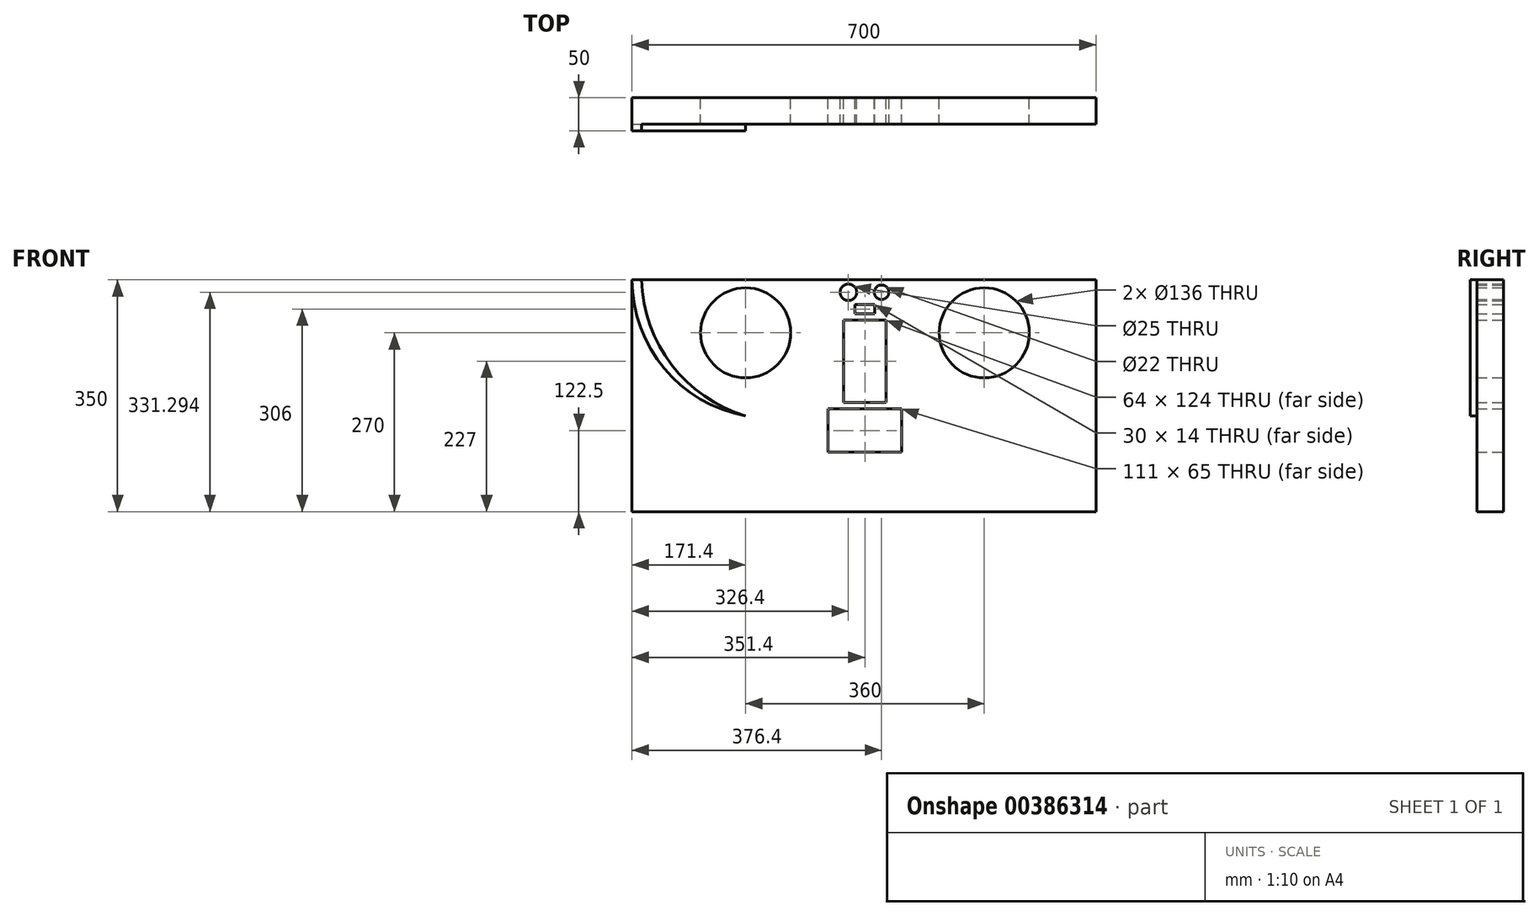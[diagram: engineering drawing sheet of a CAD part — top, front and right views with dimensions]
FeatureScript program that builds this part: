
annotation { "Feature Type Name" : "Feature", "Feature Type Description" : "" }
export const myFeature = defineFeature(function(context is Context, id is Id, definition is map)
    precondition{}
    {
        {
            var Q0;
            Q0=qCreatedBy(makeId("Front.planeOp"),FACE);
            var sketch = newSketch(context, id + "F0", { "sketchPlane" : qUnion([Q0])});
            skLineSegment(sketch, "E0.left", {"start": v(348.6, -144.5) * mm, "end": v(348.6, 205.5) * mm, "construction": true});
            skLineSegment(sketch, "E0.right", {"start": v(-351.4, -144.5) * mm, "end": v(-351.4, 205.5) * mm, "construction": true});
            skLineSegment(sketch, "E1", {"start": v(-351.4, 205.5) * mm, "end": v(-281.4, 205.5) * mm, "construction": true});
            skLineSegment(sketch, "E2", {"start": v(-281.4, 205.5) * mm, "end": v(-281.4, -74.5) * mm, "construction": true});
            skLineSegment(sketch, "E3", {"start": v(278.6, -74.5) * mm, "end": v(278.6, 205.5) * mm, "construction": true});
            skLineSegment(sketch, "E4", {"start": v(278.6, 205.5) * mm, "end": v(348.6, 205.5) * mm, "construction": true});
            skCircle(sketch, "E5", {"center": v(-180, 125.5) * mm, "radius": 68 * mm, "construction": true});
            skCircle(sketch, "E6", {"center": v(180, 125.5) * mm, "radius": 68 * mm, "construction": true});
            skLineSegment(sketch, "E7", {"start": v(0, 0) * mm, "end": v(0, 216.27) * mm, "construction": true});
            skLineSegment(sketch, "E8.bottom", {"start": v(15, 154.5) * mm, "end": v(-15, 154.5) * mm, "construction": true});
            skLineSegment(sketch, "E8.top", {"start": v(15, 168.5) * mm, "end": v(-15, 168.5) * mm, "construction": true});
            skLineSegment(sketch, "E8.left", {"start": v(15, 154.5) * mm, "end": v(15, 168.5) * mm, "construction": true});
            skLineSegment(sketch, "E8.right", {"start": v(-15, 154.5) * mm, "end": v(-15, 168.5) * mm, "construction": true});
            skPoint(sketch, "E8.middle", {"position": v(0, 161.5) * mm});
            skPoint(sketch, "E9.middle", {"position": v(0, 0) * mm});
            skCircle(sketch, "E10", {"center": v(-25, 186.8) * mm, "radius": 12.5 * mm, "construction": true});
            skCircle(sketch, "E11", {"center": v(25, 186.8) * mm, "radius": 11 * mm, "construction": true});
            skLineSegment(sketch, "E12.bottom", {"start": v(32, 20.5) * mm, "end": v(-32, 20.5) * mm, "construction": true});
            skLineSegment(sketch, "E12.top", {"start": v(32, 144.5) * mm, "end": v(-32, 144.5) * mm, "construction": true});
            skLineSegment(sketch, "E12.left", {"start": v(32, 20.5) * mm, "end": v(32, 144.5) * mm, "construction": true});
            skLineSegment(sketch, "E12.right", {"start": v(-32, 20.5) * mm, "end": v(-32, 144.5) * mm, "construction": true});
            skPoint(sketch, "E12.middle", {"position": v(0, 82.5) * mm});
            skLineSegment(sketch, "E13.bottom", {"start": v(55.5, -54.5) * mm, "end": v(-55.5, -54.5) * mm, "construction": true});
            skLineSegment(sketch, "E13.top", {"start": v(55.5, 10.5) * mm, "end": v(-55.5, 10.5) * mm, "construction": true});
            skLineSegment(sketch, "E13.left", {"start": v(55.5, -54.5) * mm, "end": v(55.5, 10.5) * mm, "construction": true});
            skLineSegment(sketch, "E13.right", {"start": v(-55.5, -54.5) * mm, "end": v(-55.5, 10.5) * mm, "construction": true});
            skPoint(sketch, "E13.middle", {"position": v(0, -22) * mm});
            skSolve(sketch);
        }
        {
            var Q0;
            Q0=qCreatedBy(makeId("Front.planeOp"),FACE);
            var sketch = newSketch(context, id + "F1", { "sketchPlane" : qUnion([Q0])});
            skLineSegment(sketch, "E14", {"start": v(-351.4, 205.5) * mm, "end": v(-351.4, -144.5) * mm});
            skLineSegment(sketch, "E15", {"start": v(348.6, -144.5) * mm, "end": v(348.6, 205.5) * mm});
            skLineSegment(sketch, "E16", {"start": v(348.6, 205.5) * mm, "end": v(278.6, 205.5) * mm});
            skLineSegment(sketch, "E17", {"start": v(-281.4, 205.5) * mm, "end": v(-351.4, 205.5) * mm});
            skLineSegment(sketch, "E18", {"start": v(-281.4, 205.5) * mm, "end": v(-281.4, -144.5) * mm});
            skLineSegment(sketch, "E19", {"start": v(-281.4, -144.5) * mm, "end": v(-351.4, -144.5) * mm});
            skLineSegment(sketch, "E20", {"start": v(278.6, 205.5) * mm, "end": v(278.6, -144.5) * mm});
            skLineSegment(sketch, "E21", {"start": v(278.6, -144.5) * mm, "end": v(348.6, -144.5) * mm});
            skLineSegment(sketch, "E22.bottom", {"start": v(-281.4, 205.5) * mm, "end": v(278.6, 205.5) * mm});
            skLineSegment(sketch, "E22.top", {"start": v(-281.4, -144.5) * mm, "end": v(278.6, -144.5) * mm});
            skCircle(sketch, "E23", {"center": v(-180, 125.5) * mm, "radius": 68 * mm});
            skCircle(sketch, "E24", {"center": v(180, 125.5) * mm, "radius": 68 * mm});
            skCircle(sketch, "E25", {"center": v(25, 186.8) * mm, "radius": 11 * mm});
            skCircle(sketch, "E26", {"center": v(-25, 186.8) * mm, "radius": 12.5 * mm});
            skLineSegment(sketch, "E27.bottom", {"start": v(32, 20.5) * mm, "end": v(-32, 20.5) * mm});
            skLineSegment(sketch, "E27.top", {"start": v(32, 144.5) * mm, "end": v(-32, 144.5) * mm});
            skLineSegment(sketch, "E27.left", {"start": v(32, 20.5) * mm, "end": v(32, 144.5) * mm});
            skLineSegment(sketch, "E27.right", {"start": v(-32, 20.5) * mm, "end": v(-32, 144.5) * mm});
            skPoint(sketch, "E27.middle", {"position": v(0, 82.5) * mm});
            skLineSegment(sketch, "E28.bottom", {"start": v(15, 154.5) * mm, "end": v(-15, 154.5) * mm});
            skLineSegment(sketch, "E28.top", {"start": v(15, 168.5) * mm, "end": v(-15, 168.5) * mm});
            skLineSegment(sketch, "E28.left", {"start": v(15, 154.5) * mm, "end": v(15, 168.5) * mm});
            skLineSegment(sketch, "E28.right", {"start": v(-15, 154.5) * mm, "end": v(-15, 168.5) * mm});
            skPoint(sketch, "E28.middle", {"position": v(0, 161.5) * mm});
            skLineSegment(sketch, "E29.bottom", {"start": v(55.5, -54.5) * mm, "end": v(-55.5, -54.5) * mm});
            skLineSegment(sketch, "E29.top", {"start": v(55.5, 10.5) * mm, "end": v(-55.5, 10.5) * mm});
            skLineSegment(sketch, "E29.left", {"start": v(55.5, -54.5) * mm, "end": v(55.5, 10.5) * mm});
            skLineSegment(sketch, "E29.right", {"start": v(-55.5, -54.5) * mm, "end": v(-55.5, 10.5) * mm});
            skPoint(sketch, "E29.middle", {"position": v(0, -22) * mm});
            skSolve(sketch);
        }
        {
            var Q0;
            Q0=makeQuery(id+"F1.imprint","IMPRINT",FACE,{"disambiguationData":[TD([[makeQuery(id+"F1.imprint","IMPRINT",EDGE,{"derivedFrom":sQuery(id+"F1.wireOp",EDGE,"E22.bottom")}),-1.0]])]});
            extrude(context, id + "F2", {"entities" : qUnion([Q0]), "depth" : 40 * mm});
        }
        {
            var Q0;
            Q0=makeQuery(id+"F1.imprint","IMPRINT",FACE,{"disambiguationData":[TD([[makeQuery(id+"F1.imprint","IMPRINT",EDGE,{"derivedFrom":sQuery(id+"F1.wireOp",EDGE,"E14")}),1.0]])]});
            var Q1;
            Q1=makeQuery(id+"F1.imprint","IMPRINT",FACE,{"disambiguationData":[TD([[makeQuery(id+"F1.imprint","IMPRINT",EDGE,{"derivedFrom":sQuery(id+"F1.wireOp",EDGE,"E15")}),1.0]])]});
            extrude(context, id + "F3", {"entities" : qUnion([Q0, Q1]), "operationType" : NewBodyOperationType.ADD, "depth" : 40 * mm});
        }
        {
            var Q0;
            Q0=makeQuery(id+"F1.imprint","IMPRINT",FACE,{"disambiguationData":[TD([[makeQuery(id+"F1.imprint","IMPRINT",EDGE,{"derivedFrom":sQuery(id+"F1.wireOp",EDGE,"E23")}),1.0]])]});
            var Q1;
            Q1=makeQuery(id+"F1.imprint","IMPRINT",FACE,{"disambiguationData":[TD([[makeQuery(id+"F1.imprint","IMPRINT",EDGE,{"derivedFrom":sQuery(id+"F1.wireOp",EDGE,"E24")}),1.0]])]});
            var Q2;
            Q2=makeQuery(id+"F1.imprint","IMPRINT",FACE,{"disambiguationData":[TD([[makeQuery(id+"F1.imprint","IMPRINT",EDGE,{"derivedFrom":sQuery(id+"F1.wireOp",EDGE,"E26")}),1.0]])]});
            var Q3;
            Q3=makeQuery(id+"F1.imprint","IMPRINT",FACE,{"disambiguationData":[TD([[makeQuery(id+"F1.imprint","IMPRINT",EDGE,{"derivedFrom":sQuery(id+"F1.wireOp",EDGE,"E25")}),1.0]])]});
            var Q4;
            Q4=makeQuery(id+"F1.imprint","IMPRINT",FACE,{"disambiguationData":[TD([[makeQuery(id+"F1.imprint","IMPRINT",EDGE,{"derivedFrom":sQuery(id+"F1.wireOp",EDGE,"E28.bottom")}),-1.0]])]});
            var Q5;
            Q5=makeQuery(id+"F1.imprint","IMPRINT",FACE,{"disambiguationData":[TD([[makeQuery(id+"F1.imprint","IMPRINT",EDGE,{"derivedFrom":sQuery(id+"F1.wireOp",EDGE,"E27.bottom")}),-1.0]])]});
            var Q6;
            Q6=makeQuery(id+"F1.imprint","IMPRINT",FACE,{"disambiguationData":[TD([[makeQuery(id+"F1.imprint","IMPRINT",EDGE,{"derivedFrom":sQuery(id+"F1.wireOp",EDGE,"E29.bottom")}),-1.0]])]});
            extrude(context, id + "F4", {"entities" : qUnion([Q0, Q1, Q2, Q3, Q4, Q5, Q6]), "operationType" : NewBodyOperationType.REMOVE, "oppositeDirection" : true, "depth" : 270 * mm});
        }
        {
            var Q0;
            {var subQ0=sQuery(id+"F1.wireOp",EDGE,"E20");var subQ1=sQuery(id+"F1.wireOp",EDGE,"E18");Q0=makeQuery(id+"F3.boolean.opBoolean","MERGE",FACE,{"derivedFrom":[makeQuery(id+"F2.opExtrude","CAP_FACE",FACE,{"disambiguationData":[OSD([sQuery(id+"F1.wireOp",EDGE,"E22.bottom"),sQuery(id+"F1.wireOp",EDGE,"E22.top"),subQ1,subQ0,sQuery(id+"F1.wireOp",EDGE,"E23"),sQuery(id+"F1.wireOp",EDGE,"E24"),sQuery(id+"F1.wireOp",EDGE,"E25"),sQuery(id+"F1.wireOp",EDGE,"E26"),sQuery(id+"F1.wireOp",EDGE,"E27.bottom"),sQuery(id+"F1.wireOp",EDGE,"E27.top"),sQuery(id+"F1.wireOp",EDGE,"E27.left"),sQuery(id+"F1.wireOp",EDGE,"E27.right"),sQuery(id+"F1.wireOp",EDGE,"E28.bottom"),sQuery(id+"F1.wireOp",EDGE,"E28.top"),sQuery(id+"F1.wireOp",EDGE,"E28.left"),sQuery(id+"F1.wireOp",EDGE,"E28.right"),sQuery(id+"F1.wireOp",EDGE,"E29.bottom"),sQuery(id+"F1.wireOp",EDGE,"E29.top"),sQuery(id+"F1.wireOp",EDGE,"E29.left"),sQuery(id+"F1.wireOp",EDGE,"E29.right")])],"isStart":false}),makeQuery(id+"F3.opExtrude","CAP_FACE",FACE,{"disambiguationData":[OSD([sQuery(id+"F1.wireOp",EDGE,"E14"),sQuery(id+"F1.wireOp",EDGE,"E17"),sQuery(id+"F1.wireOp",EDGE,"E19"),subQ1])],"isStart":false}),makeQuery(id+"F3.opExtrude","CAP_FACE",FACE,{"disambiguationData":[OSD([sQuery(id+"F1.wireOp",EDGE,"E15"),sQuery(id+"F1.wireOp",EDGE,"E16"),sQuery(id+"F1.wireOp",EDGE,"E21"),subQ0])],"isStart":false})]});}
            var sketch = newSketch(context, id + "F5", { "sketchPlane" : qUnion([Q0])});
            skPoint(sketch, "E30", {"position": v(-180, 125.5) * mm});
            skPoint(sketch, "E31", {"position": v(180, 125.5) * mm});
            skPoint(sketch, "E32", {"position": v(-180, 0) * mm});
            skPoint(sketch, "E33", {"position": v(180, 0) * mm});
            skPoint(sketch, "E34", {"position": v(-78.4, 205.5) * mm});
            skPoint(sketch, "E35", {"position": v(75.6, 205.5) * mm});
            skLineSegment(sketch, "E36", {"start": v(-78.4, 205.5) * mm, "end": v(-78.4, -144.5) * mm, "construction": true});
            skLineSegment(sketch, "E37", {"start": v(75.6, 205.5) * mm, "end": v(75.6, -144.5) * mm, "construction": true});
            skArc(sketch, "E38", {"start": v(-351.4, 205.5) * mm, "mid": v(-302.93, 71.7) * mm, "end": v(-180, 0) * mm});
            skArc(sketch, "E39", {"start": v(-180, 0) * mm, "mid": v(-299.3, -32.4) * mm, "end": v(-351.4, -144.5) * mm});
            skArc(sketch, "E40", {"start": v(-180, 0) * mm, "mid": v(-105.19, 90.88) * mm, "end": v(-78.4, 205.5) * mm});
            skArc(sketch, "E41", {"start": v(-78.4, -144.5) * mm, "mid": v(-106.34, -56.18) * mm, "end": v(-180, 0) * mm});
            skArc(sketch, "E42", {"start": v(180, 0) * mm, "mid": v(301.05, 72.6) * mm, "end": v(348.6, 205.5) * mm});
            skArc(sketch, "E43", {"start": v(348.6, -144.5) * mm, "mid": v(297.53, -33.48) * mm, "end": v(180, 0) * mm});
            skArc(sketch, "E44", {"start": v(75.6, 205.5) * mm, "mid": v(103.2, 90.25) * mm, "end": v(180, 0) * mm});
            skArc(sketch, "E45", {"start": v(180, 0) * mm, "mid": v(104.43, -55.36) * mm, "end": v(75.6, -144.5) * mm});
            skArc(sketch, "E46", {"start": v(-337.03, 205.5) * mm, "mid": v(-291.72, 77.38) * mm, "end": v(-180, 0) * mm});
            skArc(sketch, "E47", {"start": v(-180, 0) * mm, "mid": v(-260.12, -52.78) * mm, "end": v(-231.96, -144.5) * mm});
            skArc(sketch, "E48", {"start": v(-180, 0) * mm, "mid": v(-115.4, 92.85) * mm, "end": v(-105.19, 205.5) * mm});
            skPoint(sketch, "E48.endSnap0", {"position": v(-105.19, 90.88) * mm});
            skArc(sketch, "E49", {"start": v(-204.8, -144.5) * mm, "mid": v(-134.1, -82.25) * mm, "end": v(-180, 0) * mm});
            skArc(sketch, "E50", {"start": v(180, 0) * mm, "mid": v(287.56, 78.99) * mm, "end": v(330.04, 205.5) * mm});
            skPoint(sketch, "E51", {"position": v(102.38, 205.5) * mm});
            skArc(sketch, "E52", {"start": v(102.38, 205.5) * mm, "mid": v(113.85, 92.42) * mm, "end": v(180, 0) * mm});
            skArc(sketch, "E53", {"start": v(227.8, -144.5) * mm, "mid": v(256.43, -54.88) * mm, "end": v(180, 0) * mm});
            skArc(sketch, "E54", {"start": v(180, 0) * mm, "mid": v(133.6, -81.17) * mm, "end": v(202.37, -144.5) * mm});
            skLineSegment(sketch, "E55", {"start": v(-351.4, -144.5) * mm, "end": v(-231.96, -144.5) * mm});
            skLineSegment(sketch, "E56", {"start": v(-204.8, -144.5) * mm, "end": v(-78.4, -144.5) * mm});
            skLineSegment(sketch, "E57", {"start": v(-351.4, 205.5) * mm, "end": v(-337.03, 205.5) * mm});
            skLineSegment(sketch, "E58", {"start": v(-105.19, 205.5) * mm, "end": v(-78.4, 205.5) * mm});
            skLineSegment(sketch, "E59", {"start": v(75.6, 205.5) * mm, "end": v(102.38, 205.5) * mm});
            skLineSegment(sketch, "E60", {"start": v(330.04, 205.5) * mm, "end": v(348.6, 205.5) * mm});
            skLineSegment(sketch, "E61", {"start": v(75.6, -144.5) * mm, "end": v(202.37, -144.5) * mm});
            skLineSegment(sketch, "E62", {"start": v(227.8, -144.5) * mm, "end": v(348.6, -144.5) * mm});
            skSolve(sketch);
        }
        {
            var Q0;
            Q0=makeQuery(id+"F5.imprint","IMPRINT",FACE,{"disambiguationData":[TD([[makeQuery(id+"F5.imprint","IMPRINT",EDGE,{"derivedFrom":sQuery(id+"F5.wireOp",EDGE,"E38")}),1.0]])]});
            extrude(context, id + "F6", {"entities" : qUnion([Q0]), "operationType" : NewBodyOperationType.ADD, "depth" : 10 * mm});
        }
    });
